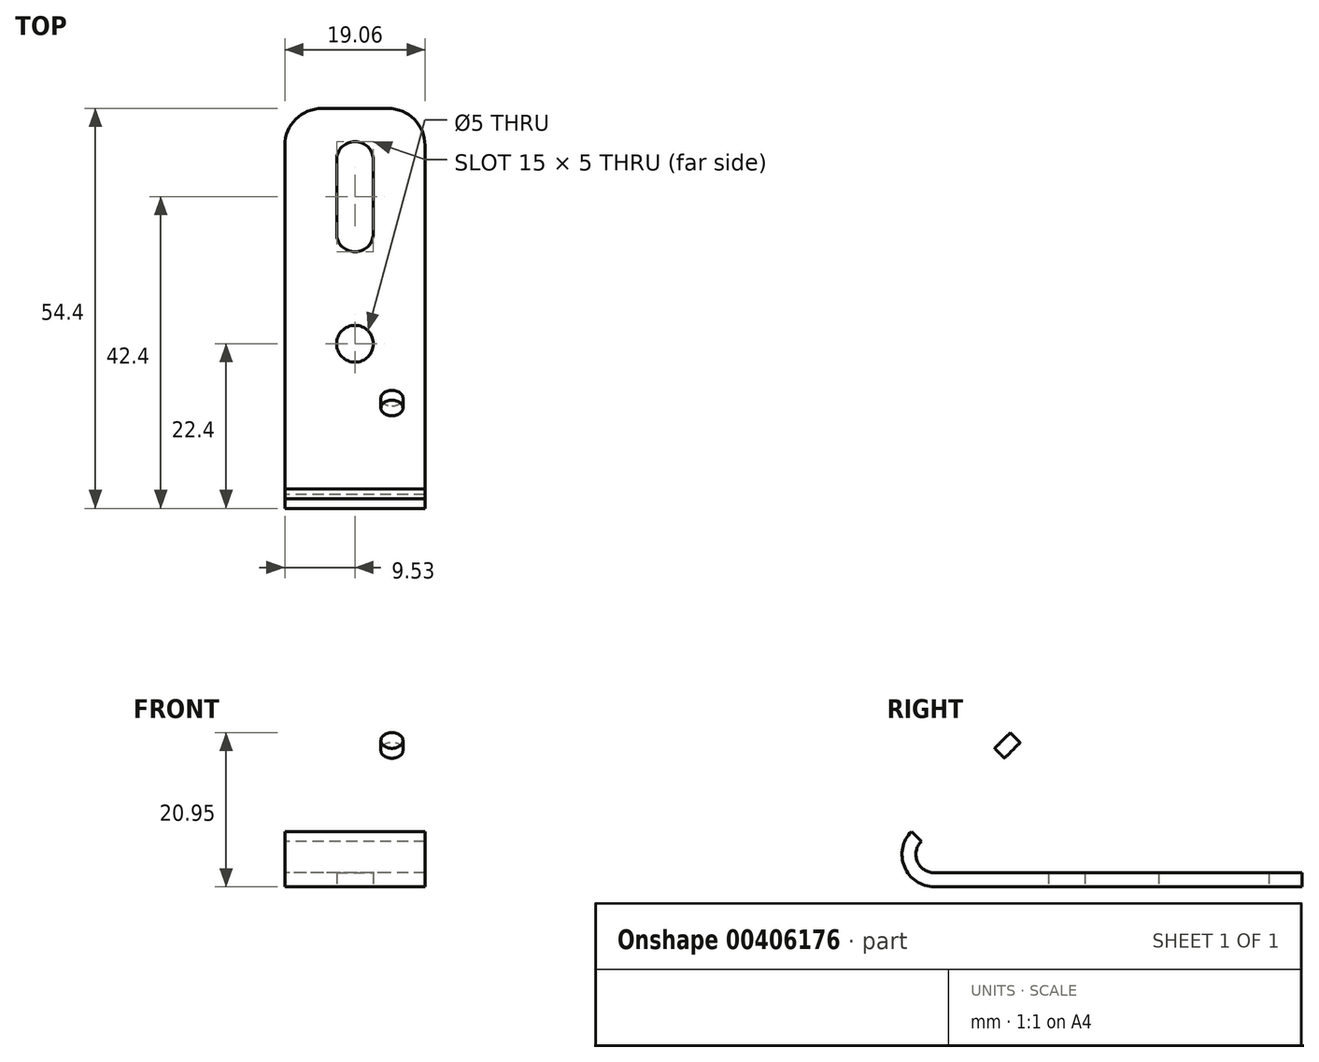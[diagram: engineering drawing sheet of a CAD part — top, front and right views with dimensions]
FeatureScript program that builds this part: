
annotation { "Feature Type Name" : "Feature", "Feature Type Description" : "" }
export const myFeature = defineFeature(function(context is Context, id is Id, definition is map)
    precondition{}
    {
        {
            var Q0;
            Q0=qCreatedBy(makeId("Right.planeOp"),FACE);
            var sketch = newSketch(context, id + "F0", { "sketchPlane" : qUnion([Q0])});
            skLineSegment(sketch, "E0", {"start": v(0, 0) * mm, "end": v(50, 0) * mm});
            skCircle(sketch, "E1", {"center": v(0, 4.4) * mm, "radius": 4.4 * mm, "construction": true});
            skLineSegment(sketch, "E2", {"start": v(-3.11, 7.51) * mm, "end": v(14.57, 25.19) * mm});
            skArc(sketch, "E3", {"start": v(0, 0) * mm, "mid": v(-4.07, 2.72) * mm, "end": v(-3.11, 7.51) * mm});
            skLineSegment(sketch, "E4.0", {"start": v(-1.77, 6.17) * mm, "end": v(15.9, 23.85) * mm});
            skArc(sketch, "E4.1", {"start": v(0, 1.9) * mm, "mid": v(-2.3, 3.44) * mm, "end": v(-1.77, 6.17) * mm});
            skLineSegment(sketch, "E4.2", {"start": v(0, 1.9) * mm, "end": v(50, 1.9) * mm});
            skLineSegment(sketch, "E5", {"start": v(15.9, 23.85) * mm, "end": v(14.57, 25.19) * mm});
            skLineSegment(sketch, "E6", {"start": v(50, 0) * mm, "end": v(50, 1.9) * mm});
            skSolve(sketch);
        }
        {
            var Q0;
            Q0 = qSketchRegion(id + "F0", true);
            extrude(context, id + "F1", {"entities" : qUnion([Q0]), "endBound" : BoundingType.SYMMETRIC, "depth" : 19.05 * mm});
        }
        {
            var Q0;
            Q0=makeQuery(id+"F1.opExtrude","SWEPT_FACE",FACE,{"disambiguationData":[OSD([sQuery(id+"F0.wireOp",EDGE,"E0")])]});
            var sketch = newSketch(context, id + "F2", { "sketchPlane" : qUnion([Q0])});
            skCircle(sketch, "E7", {"center": v(0, -43) * mm, "radius": 2.5 * mm});
            skPoint(sketch, "E7.centerSnap0", {"position": v(0, -50) * mm});
            skCircle(sketch, "E8", {"center": v(0, -33) * mm, "radius": 2.5 * mm});
            skCircle(sketch, "E9", {"center": v(0, -18) * mm, "radius": 2.5 * mm});
            skLineSegment(sketch, "E10.bottom", {"start": v(-2.5, -33) * mm, "end": v(2.5, -33) * mm});
            skLineSegment(sketch, "E10.top", {"start": v(-2.5, -43) * mm, "end": v(2.5, -43) * mm});
            skLineSegment(sketch, "E10.left", {"start": v(-2.5, -33) * mm, "end": v(-2.5, -43) * mm});
            skLineSegment(sketch, "E10.right", {"start": v(2.5, -33) * mm, "end": v(2.5, -43) * mm});
            skSolve(sketch);
        }
        {
            var Q0;
            {var subQ0=sQuery(id+"F2.wireOp",EDGE,"E10.top");Q0=makeQuery(id+"F2.imprint","IMPRINT",FACE,{"disambiguationData":[TD([[makeQuery(id+"F2.imprint","IMPRINT",EDGE,{"derivedFrom":subQ0}),-1.0]])]});}
            var Q1;
            {var subQ0=sQuery(id+"F2.wireOp",EDGE,"E10.top");Q1=makeQuery(id+"F2.imprint","IMPRINT",FACE,{"disambiguationData":[TD([[makeQuery(id+"F2.imprint","IMPRINT",EDGE,{"derivedFrom":subQ0}),1.0]])]});}
            var Q2;
            {var subQ0=sQuery(id+"F2.wireOp",EDGE,"E10.left");Q2=makeQuery(id+"F2.imprint","IMPRINT",FACE,{"disambiguationData":[TD([[makeQuery(id+"F2.imprint","IMPRINT",EDGE,{"derivedFrom":subQ0}),1.0]])]});}
            var Q3;
            {var subQ0=sQuery(id+"F2.wireOp",EDGE,"E10.bottom");Q3=makeQuery(id+"F2.imprint","IMPRINT",FACE,{"disambiguationData":[TD([[makeQuery(id+"F2.imprint","IMPRINT",EDGE,{"derivedFrom":subQ0}),1.0]])]});}
            var Q4;
            {var subQ0=sQuery(id+"F2.wireOp",EDGE,"E10.bottom");Q4=makeQuery(id+"F2.imprint","IMPRINT",FACE,{"disambiguationData":[TD([[makeQuery(id+"F2.imprint","IMPRINT",EDGE,{"derivedFrom":subQ0}),-1.0]])]});}
            var Q5;
            Q5=makeQuery(id+"F2.imprint","IMPRINT",FACE,{"disambiguationData":[TD([[makeQuery(id+"F2.imprint","IMPRINT",EDGE,{"derivedFrom":sQuery(id+"F2.wireOp",EDGE,"E9")}),1.0]])]});
            var Q6;
            Q6=makeQuery(id+"F1.opExtrude","SWEPT_FACE",FACE,{"disambiguationData":[OSD([sQuery(id+"F0.wireOp",EDGE,"E4.2")])]});
            extrude(context, id + "F3", {"entities" : qUnion([Q0, Q1, Q2, Q3, Q4, Q5]), "operationType" : NewBodyOperationType.REMOVE, "endBound" : BoundingType.UP_TO_SURFACE, "oppositeDirection" : true, "endBoundEntityFace" : qUnion([Q6]), "depth" : 25.4 * mm});
        }
        {
            var Q0;
            Q0=makeQuery(id+"F1.opExtrude","SWEPT_FACE",FACE,{"disambiguationData":[OSD([sQuery(id+"F0.wireOp",EDGE,"E2")])]});
            var sketch = newSketch(context, id + "F4", { "sketchPlane" : qUnion([Q0])});
            skLineSegment(sketch, "E11", {"start": v(0, 28.11) * mm, "end": v(0, 3.11) * mm, "construction": true});
            skCircle(sketch, "E12", {"center": v(-5.03, 20.61) * mm, "radius": 1.5 * mm});
            skCircle(sketch, "E13.MirrorC", {"center": v(5.03, 20.61) * mm, "radius": 1.5 * mm});
            skSolve(sketch);
        }
        {
            var Q0;
            Q0=makeQuery(id+"F4.imprint","IMPRINT",FACE,{"disambiguationData":[TD([[makeQuery(id+"F4.imprint","IMPRINT",EDGE,{"derivedFrom":sQuery(id+"F4.wireOp",EDGE,"E12")}),1.0]])]});
            var Q1;
            Q1=makeQuery(id+"F4.imprint","IMPRINT",FACE,{"disambiguationData":[TD([[makeQuery(id+"F4.imprint","IMPRINT",EDGE,{"derivedFrom":sQuery(id+"F4.wireOp",EDGE,"E13.MirrorC")}),-1.0]])]});
            var Q2;
            Q2=makeQuery(id+"F1.opExtrude","SWEPT_FACE",FACE,{"disambiguationData":[OSD([sQuery(id+"F0.wireOp",EDGE,"E4.0")])]});
            extrude(context, id + "F5", {"entities" : qUnion([Q0, Q1]), "operationType" : NewBodyOperationType.REMOVE, "endBound" : BoundingType.UP_TO_SURFACE, "oppositeDirection" : true, "endBoundEntityFace" : qUnion([Q2]), "depth" : 25.4 * mm});
        }
        {
            var Q0;
            Q0=makeQuery(id+"F1.opExtrude","CAP_EDGE",EDGE,{"disambiguationData":[OSD([sQuery(id+"F0.wireOp",EDGE,"E5")])],"isStart":false});
            var Q1;
            Q1=makeQuery(id+"F1.opExtrude","CAP_EDGE",EDGE,{"disambiguationData":[OSD([sQuery(id+"F0.wireOp",EDGE,"E5")])],"isStart":true});
            var Q2;
            Q2=makeQuery(id+"F1.opExtrude","CAP_EDGE",EDGE,{"disambiguationData":[OSD([sQuery(id+"F0.wireOp",EDGE,"E6")])],"isStart":false});
            var Q3;
            Q3=makeQuery(id+"F1.opExtrude","CAP_EDGE",EDGE,{"disambiguationData":[OSD([sQuery(id+"F0.wireOp",EDGE,"E6")])],"isStart":true});
            fillet(context, id + "F6", {"entities" : qUnion([Q0, Q1, Q2, Q3]), "radius" : 5 * mm, "tangentPropagation" : true, "allowEdgeOverflow" : false});
        }
    });
